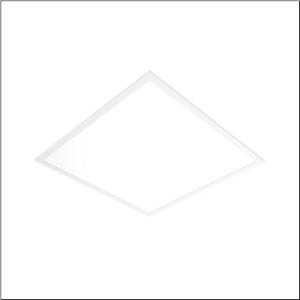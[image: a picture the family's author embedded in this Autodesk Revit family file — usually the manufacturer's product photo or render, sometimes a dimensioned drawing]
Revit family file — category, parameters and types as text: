
# Revit family: apollon_r__41_51mh12wd2443_fb74
name_source: partatom
category: Lighting Fixtures
units: mm (PartAtom-declared; Revit-internal decimal feet)

## family parameters
Cut with Voids When Loaded = No
Host = Face
Light Source = No
Part Type = Normal
Room Calculation Point = No
Round Connector Dimension = Use Diameter
Shared = No

## types (1)
- Apollon® 41 (1 x LED, 3500 lm, 28.5 W, 4000K)
    Apparent Load = 29 VA
    CIE Flux Codes = 61 87 97 100 100
    Color Rendering = 80
    Color Temperature = 4000K
    Default Elevation = 1800 mm
    Description = Apollon® 41, office luminaire, primary optical cover: prismatic diffuser, of PS, light emission: direct distribution, primary light characteristic: symmetric, installation type: lay-in mounting, LED, rated luminous flux: 3.500lm, luminous efficacy: 123lm/W, light colour: 840, colour temperature: 4000K, with terminal, 5-pole, mains connection: 220..240V, AC/DC, 0/50..60Hz, housing, of aluminium section, traffic white (RAL 9016), module: M600, length: 600mm, width: 600mm, height: 28mm, housing upper side, of sheet steel, protection rating (complete): IP20, protection rating (lamp compartment, on room side): IP40, insulation class (complete): insulation class II (safety insulation), certification: CE, ENEC, permissible operating ambient temperature: -25..+40°C, packaging unit: 1 piece
    Height = 0 mm  [stored 0 ft]
    Lamp = 1 x LED
    Lamp Light Flux = 3500 lm
    Lamp Power = 28.5 W
    Lamp count = 1
    Length = 600 mm
    Luminous efficacy = 123 lm/W
    Manufacturer = Siteco
    ModVariant = No
    Model = 51MH12WD2443
    Mounting Place = Ceiling
    Mounting Type = Recessed
    Number of Poles = 1
    OnlyDefault = Yes
    Power Factor = 1
    Product Name = Apollon® 41
    Product group = office luminaire | ceiling recessed
    ProductGroupID = 401
    Protection Class = Protection class II
    Protection Degree = IP 20
    RLX_Detail_Level = 1
    RLX_Emergency_Light_Flux = 0 lm
    RLX_Emergency_Type = 0
    RLX_Emergency_Type_DB = No
    RlxData = <blob elided: 12193 chars, md5=789db00d>
    Socket = socket
    Standby Power = 0 W
    System Light Flux = 3500 lm
    System Power = 29 W
    Type Comments = Product without accessories
    Type Image = l_1291024.jpg
    URL = http://relux.com
    VarID = ---
    Voltage = 0 V
    Weight = 0.00 kg
    Width = 600 mm

note: [stored X ft] marks values corroborated as IEEE doubles in the binary element streams (Revit-internal decimal feet)

## geometry (parser evidence)
native form markers: Sweep x12
no freeform markers — native parametric forms only
